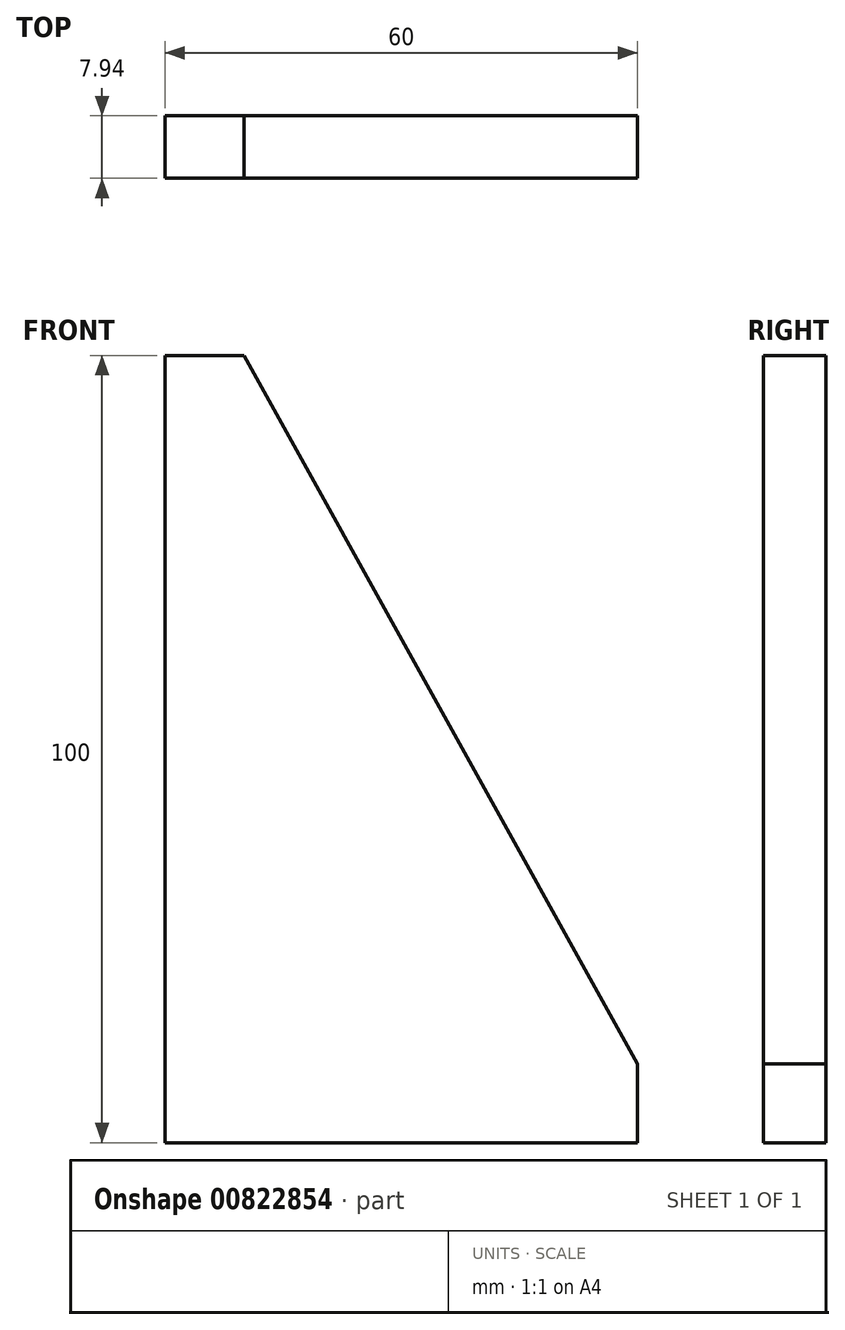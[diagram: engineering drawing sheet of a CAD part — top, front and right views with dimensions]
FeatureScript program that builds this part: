
annotation { "Feature Type Name" : "Feature", "Feature Type Description" : "" }
export const myFeature = defineFeature(function(context is Context, id is Id, definition is map)
    precondition{}
    {
        {
            var Q0;
            Q0=qCreatedBy(makeId("Front.planeOp"),FACE);
            var sketch = newSketch(context, id + "F0", { "sketchPlane" : qUnion([Q0])});
            skLineSegment(sketch, "E0", {"start": v(0, 0) * mm, "end": v(0, 100) * mm});
            skLineSegment(sketch, "E1", {"start": v(60, 0) * mm, "end": v(0, 0) * mm});
            skLineSegment(sketch, "E2", {"start": v(0, 100) * mm, "end": v(10, 100) * mm});
            skLineSegment(sketch, "E3", {"start": v(10, 100) * mm, "end": v(60, 10) * mm});
            skLineSegment(sketch, "E4", {"start": v(60, 10) * mm, "end": v(60, 0) * mm});
            skSolve(sketch);
        }
        {
            var Q0;
            Q0 = qSketchRegion(id + "F0", true);
            extrude(context, id + "F1", {"entities" : qUnion([Q0]), "depth" : (5 * 25.4 / 16) * mm, "offsetDistance" : 25 * mm});
        }
    });
